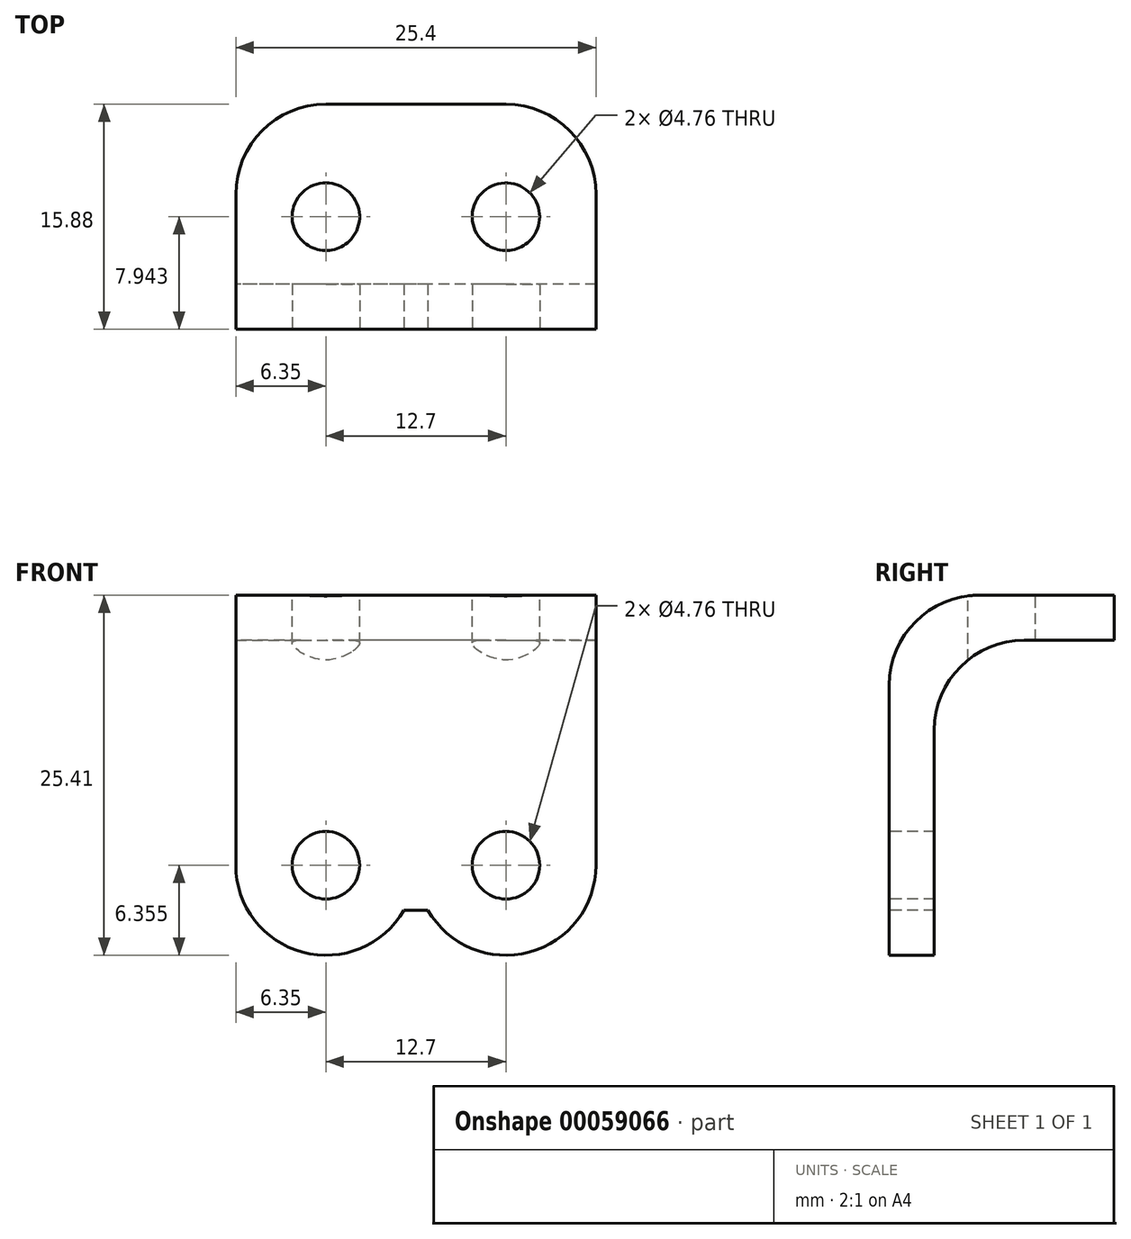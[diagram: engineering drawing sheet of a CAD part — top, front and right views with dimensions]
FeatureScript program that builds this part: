
annotation { "Feature Type Name" : "Feature", "Feature Type Description" : "" }
export const myFeature = defineFeature(function(context is Context, id is Id, definition is map)
    precondition{}
    {
        {
            var Q0;
            Q0=qCreatedBy(makeId("Right.planeOp"),FACE);
            var sketch = newSketch(context, id + "F0", { "sketchPlane" : qUnion([Q0])});
            skLineSegment(sketch, "E0", {"start": v(12.7, 0) * mm, "end": v(0, 0) * mm});
            skLineSegment(sketch, "E1", {"start": v(0, 0) * mm, "end": v(0, -25.4) * mm});
            skLineSegment(sketch, "E2.0", {"start": v(-3.18, 3.17) * mm, "end": v(-3.17, -25.4) * mm});
            skLineSegment(sketch, "E2.1", {"start": v(12.7, 3.18) * mm, "end": v(-3.18, 3.17) * mm});
            skLineSegment(sketch, "E3", {"start": v(12.7, 3.18) * mm, "end": v(12.7, 0) * mm});
            skLineSegment(sketch, "E4", {"start": v(0, -25.4) * mm, "end": v(-3.17, -25.4) * mm});
            skSolve(sketch);
        }
        {
            var Q0;
            Q0 = qSketchRegion(id + "F0", true);
            extrude(context, id + "F1", {"entities" : qUnion([Q0]), "depth" : 25.4 * mm});
        }
        {
            var Q0;
            Q0=makeQuery(id+"F1.opExtrude","SWEPT_FACE",FACE,{"disambiguationData":[OSD([sQuery(id+"F0.wireOp",EDGE,"E2.1")])]});
            var sketch = newSketch(context, id + "F2", { "sketchPlane" : qUnion([Q0])});
            skLineSegment(sketch, "E5", {"start": v(0, 4.76) * mm, "end": v(25.4, 4.76) * mm, "construction": true});
            skLineSegment(sketch, "E6", {"start": v(12.7, -3.18) * mm, "end": v(12.7, 12.7) * mm, "construction": true});
            skLineSegment(sketch, "E7", {"start": v(12.7, 17.67) * mm, "end": v(0, 17.67) * mm, "construction": true});
            skLineSegment(sketch, "E8", {"start": v(6.35, 17.67) * mm, "end": v(6.35, -3.18) * mm, "construction": true});
            skLineSegment(sketch, "E9", {"start": v(12.7, 17.67) * mm, "end": v(25.4, 17.67) * mm, "construction": true});
            skLineSegment(sketch, "E10", {"start": v(19.05, 17.67) * mm, "end": v(19.05, -3.18) * mm, "construction": true});
            skCircle(sketch, "E11", {"center": v(6.35, 4.76) * mm, "radius": 2.38 * mm});
            skCircle(sketch, "E12", {"center": v(19.05, 4.76) * mm, "radius": 2.38 * mm});
            skSolve(sketch);
        }
        {
            var Q0;
            Q0 = qSketchRegion(id + "F2", true);
            extrude(context, id + "F3", {"entities" : qUnion([Q0]), "operationType" : NewBodyOperationType.REMOVE, "endBound" : BoundingType.THROUGH_ALL, "oppositeDirection" : true, "depth" : 25.4 * mm});
        }
        {
            var Q0;
            Q0=makeQuery(id+"F1.opExtrude","SWEPT_FACE",FACE,{"disambiguationData":[OSD([sQuery(id+"F0.wireOp",EDGE,"E2.0")])]});
            var sketch = newSketch(context, id + "F4", { "sketchPlane" : qUnion([Q0])});
            skLineSegment(sketch, "E13", {"start": v(25.4, -30.99) * mm, "end": v(12.7, -30.99) * mm, "construction": true});
            skPoint(sketch, "E13.endSnap0", {"position": v(12.7, -25.4) * mm});
            skLineSegment(sketch, "E14", {"start": v(12.7, -30.99) * mm, "end": v(0, -30.99) * mm, "construction": true});
            skLineSegment(sketch, "E15", {"start": v(6.35, -30.99) * mm, "end": v(6.35, 3.17) * mm, "construction": true});
            skLineSegment(sketch, "E16", {"start": v(19.05, -30.99) * mm, "end": v(19.05, 3.18) * mm, "construction": true});
            skLineSegment(sketch, "E17", {"start": v(0, -15.88) * mm, "end": v(25.4, -15.88) * mm, "construction": true});
            skPoint(sketch, "E17.endSnap0", {"position": v(25.4, -11.11) * mm});
            skCircle(sketch, "E18", {"center": v(19.05, -15.88) * mm, "radius": 2.38 * mm});
            skPoint(sketch, "E18.centerSnap0", {"position": v(19.05, -13.9) * mm});
            skCircle(sketch, "E19", {"center": v(6.35, -15.88) * mm, "radius": 2.38 * mm});
            skCircle(sketch, "E20.0", {"center": v(6.35, -15.88) * mm, "radius": 6.35 * mm});
            skCircle(sketch, "E21.0", {"center": v(19.05, -15.88) * mm, "radius": 6.35 * mm});
            skLineSegment(sketch, "E22", {"start": v(6.35, -22.23) * mm, "end": v(19.05, -22.23) * mm, "construction": true});
            skLineSegment(sketch, "E23", {"start": v(12.7, -22.23) * mm, "end": v(12.7, -15.88) * mm, "construction": true});
            skLineSegment(sketch, "E24", {"start": v(11.85, -19.05) * mm, "end": v(13.55, -19.05) * mm});
            skPoint(sketch, "E24.startSnap0", {"position": v(12.7, -19.05) * mm});
            skSolve(sketch);
        }
        {
            var Q0;
            {var subQ0=sQuery(id+"F0.wireOp",EDGE,"E2.0");var subQ2=makeQuery(id+"F1.opExtrude","SWEPT_EDGE",EDGE,{"disambiguationData":[OSD([subQ0,sQuery(id+"F0.wireOp",EDGE,"E4")])]});Q0=makeQuery(id+"F4.imprint","IMPRINT",FACE,{"disambiguationData":[TD([[makeQuery(id+"F4.imprint","IMPRINT",EDGE,{"derivedFrom":subQ2}),-1.0]])]});}
            var Q1;
            Q1=makeQuery(id+"F4.imprint","IMPRINT",FACE,{"disambiguationData":[TD([[makeQuery(id+"F4.imprint","IMPRINT",EDGE,{"derivedFrom":sQuery(id+"F4.wireOp",EDGE,"E18")}),1.0]])]});
            var Q2;
            Q2=makeQuery(id+"F4.imprint","IMPRINT",FACE,{"disambiguationData":[TD([[makeQuery(id+"F4.imprint","IMPRINT",EDGE,{"derivedFrom":sQuery(id+"F4.wireOp",EDGE,"E19")}),1.0]])]});
            extrude(context, id + "F5", {"entities" : qUnion([Q0, Q1, Q2]), "operationType" : NewBodyOperationType.REMOVE, "endBound" : BoundingType.THROUGH_ALL, "oppositeDirection" : true, "depth" : 25.4 * mm});
        }
        {
            var Q0;
            Q0=makeQuery(id+"F1.opExtrude","SWEPT_EDGE",EDGE,{"disambiguationData":[OSD([sQuery(id+"F0.wireOp",EDGE,"E2.0"),sQuery(id+"F0.wireOp",EDGE,"E2.1")])]});
            var Q1;
            Q1=makeQuery(id+"F1.opExtrude","CAP_EDGE",EDGE,{"disambiguationData":[OSD([sQuery(id+"F0.wireOp",EDGE,"E3")])],"isStart":true});
            var Q2;
            Q2=makeQuery(id+"F1.opExtrude","CAP_EDGE",EDGE,{"disambiguationData":[OSD([sQuery(id+"F0.wireOp",EDGE,"E3")])],"isStart":false});
            var Q3;
            Q3=makeQuery(id+"F1.opExtrude","SWEPT_EDGE",EDGE,{"disambiguationData":[OSD([sQuery(id+"F0.wireOp",EDGE,"E0"),sQuery(id+"F0.wireOp",EDGE,"E1")])]});
            fillet(context, id + "F6", {"entities" : qUnion([Q0, Q1, Q2, Q3]), "radius" : 6.35 * mm, "tangentPropagation" : true, "allowEdgeOverflow" : false});
        }
    });
